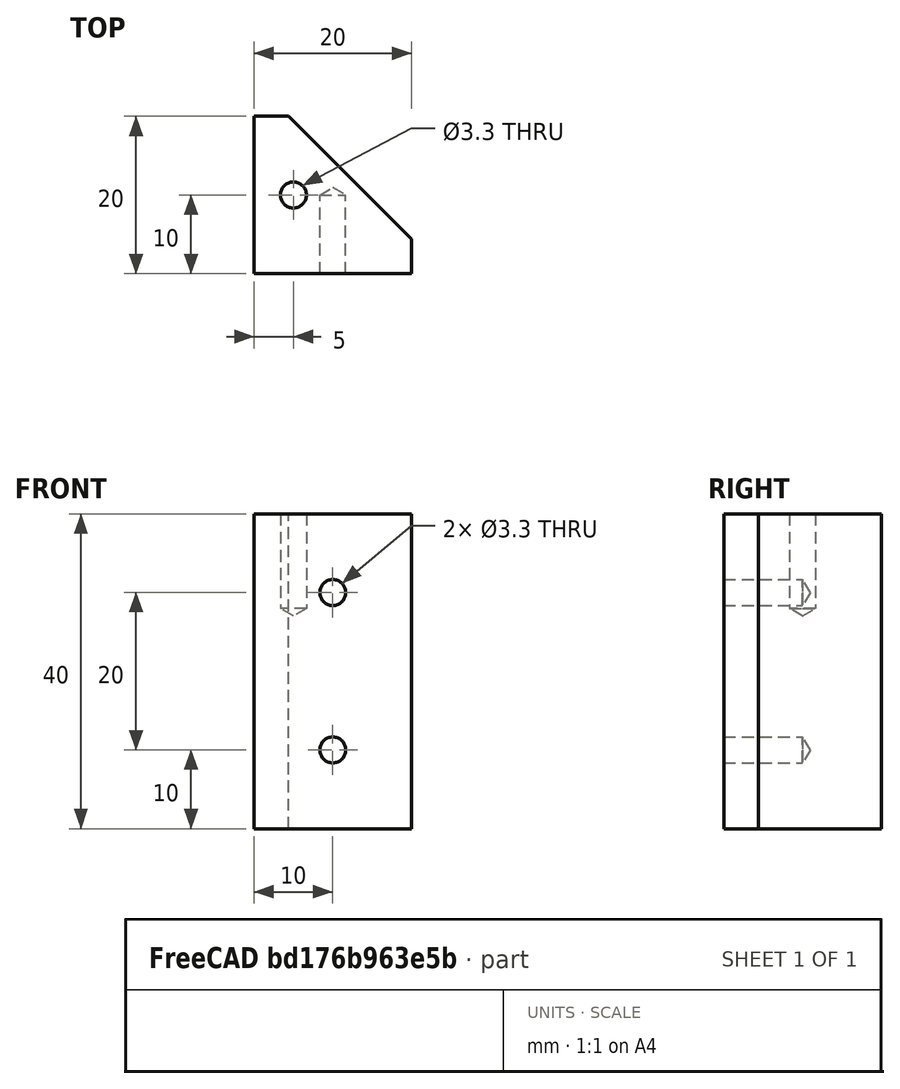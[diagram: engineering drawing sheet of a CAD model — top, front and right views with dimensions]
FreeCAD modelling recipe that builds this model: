
FCSTD DOCUMENT  (FreeCAD 1.0R39319 (Git))
Label: OCT-URBLK-AA
License: Creative Commons Attribution 4.0
LicenseURL: https://creativecommons.org/licenses/by/4.0/
objects: TechDraw::DrawViewDimension×9, Sketcher::SketchObject×3, PartDesign::Hole×2, TechDraw::DrawProjGroupItem×2, PartDesign::Pad×1, PartDesign::Body×1, TechDraw::DrawSVGTemplate×1, TechDraw::DrawProjGroup×1, TechDraw::DrawPage×1
note: 29 computed .brp shape members not serialized (recipe doc carries the construction recipe); baked Part::Feature solids carry a one-line shape summary decoded from their .brp

FEATURE [Sketcher::SketchObject] Sketch
  ArcFitTolerance = 1e-06
  AttachmentSupport = -> [XY_Plane]
  FullyConstrained = true
  MakeInternals = false
  MapMode = 5
  sketch-geometry (5):
    g0: LineSegment StartX=65 StartY=0 StartZ=0 EndX=85 EndY=0 EndZ=0
    g1: LineSegment StartX=85 StartY=0 StartZ=0 EndX=85 EndY=4.4 EndZ=0
    g2: LineSegment StartX=65 StartY=20 StartZ=0 EndX=65 EndY=0 EndZ=0
    g3: LineSegment StartX=65 StartY=20 StartZ=0 EndX=69.4 EndY=20 EndZ=0
    g4: LineSegment StartX=69.4 StartY=20 StartZ=0 EndX=85 EndY=4.4 EndZ=0
  constraints (15):
    c: PointOnObject(g0,g-1)
    c: PointOnObject(g0,g-1)
    c: Coincident(g0,g1)
    c: Vertical(g1)
    c: Vertical(g2)
    c: DistanceX(g0,g0) = 20
    c: DistanceX(g-1,g0) = 85
    c: Coincident(g2,g0)
    c: DistanceY(g2,g2) = 20
    c: Coincident(g2,g3)
    c: Horizontal(g3)
    c: Coincident(g3,g4)
    c: Coincident(g4,g1)
    c: Angle(g4,g0) = 0.785398
    c: DistanceY(g1,g1) = 4.4
FEATURE [PartDesign::Pad] Pad
  Direction = (0,0,1)
  Length = 40
  Length2 = 10
  Profile = -> Sketch
  ReferenceAxis = -> Sketch [N_Axis]
  Suppressed = false
  Type = 0
FEATURE [Sketcher::SketchObject] Sketch001
  ArcFitTolerance = 1e-06
  AttachmentSupport = -> [Pad]
  FullyConstrained = true
  MakeInternals = false
  MapMode = 5
  Placement = pos=(0,0,0) rot=(1,0,0;1.5708rad)
  sketch-geometry (3):
    g0: Circle CenterX=75 CenterY=30 CenterZ=0 NormalX=0 NormalY=0 NormalZ=1 AngleXU=0 Radius=2
    g1: Circle CenterX=75 CenterY=10 CenterZ=0 NormalX=0 NormalY=0 NormalZ=1 AngleXU=0 Radius=2
    g2: LineSegment [constr] StartX=75 StartY=30 StartZ=0 EndX=75 EndY=10 EndZ=0
  constraints (8):
    c: Coincident(g2,g0)
    c: Coincident(g2,g1)
    c: Vertical(g2)
    c: Equal(g0,g1)
    c: Diameter(g0) = 4
    c: DistanceX(g-1,g1) = 75
    c: Distance(g1,g-1) = 10
    c: DistanceY(g2,g2) = 20
FEATURE [PartDesign::Hole] Hole
  BaseFeature = -> Pad
  CustomThreadClearance = 0
  Depth = 10
  DepthType = 0
  Diameter = 3.3
  DrillForDepth = false
  DrillPoint = 1
  DrillPointAngle = 118
  HoleCutCountersinkAngle = 90
  HoleCutCustomValues = false
  HoleCutDepth = 0
  HoleCutDiameter = 6.1
  HoleCutType = 0
  ModelThread = false
  Profile = -> Sketch001
  Suppressed = false
  Tapered = false
  TaperedAngle = 90
  ThreadClass = 0
  ThreadDepth = 10
  ThreadDepthType = 0
  ThreadDirection = 0
  ThreadFit = 0
  ThreadSize = 11
  ThreadType = 1
  Threaded = true
  UseCustomThreadClearance = false
FEATURE [Sketcher::SketchObject] Sketch002
  ArcFitTolerance = 1e-06
  AttachmentSupport = -> [Hole]
  FullyConstrained = true
  MakeInternals = false
  MapMode = 5
  Placement = pos=(0,0,40) rot=(0,0,1;0rad)
  sketch-geometry (1):
    g0: Circle CenterX=70 CenterY=10 CenterZ=0 NormalX=0 NormalY=0 NormalZ=1 AngleXU=0 Radius=2
  constraints (3):
    c: Diameter(g0) = 4
    c: Distance(g0,g-2) = 70
    c: Distance(g0,g-1) = 10
FEATURE [PartDesign::Hole] Hole001
  BaseFeature = -> Hole
  CustomThreadClearance = 0
  Depth = 12
  DepthType = 0
  Diameter = 3.3
  DrillForDepth = false
  DrillPoint = 1
  DrillPointAngle = 118
  HoleCutCountersinkAngle = 90
  HoleCutCustomValues = false
  HoleCutDepth = 0
  HoleCutDiameter = 6.1
  HoleCutType = 0
  ModelThread = false
  Profile = -> Sketch002
  Suppressed = false
  Tapered = false
  TaperedAngle = 90
  ThreadClass = 0
  ThreadDepth = 12
  ThreadDepthType = 0
  ThreadDirection = 0
  ThreadFit = 0
  ThreadSize = 11
  ThreadType = 1
  Threaded = true
  UseCustomThreadClearance = false
FEATURE [PartDesign::Body] Body  label="upper right block"
  AllowCompound = false
  Group = -> [Sketch,Pad,Sketch001,Hole,Sketch002,Hole001]
  Origin = -> Origin
  Tip = -> Hole001
FEATURE [TechDraw::DrawSVGTemplate] Template
  EditableTexts = approval_person=S. Aphelion; creator=Michael Stoll; date_of_issue=08/02/2026; document_status=In preparation; document_type=Component Drawing; drawing_number=DN; general_tolerances=ISO 2768-m; language_code=EN; part_material=Aluminium 6082 T6; responsible_department=RD; revision_index=A; scale=2 : 1; sheet_number=1 / 1; supplementary_title_1=Upper Right Panel Block; title=OCT-URBLK-AA
  Height = 297
  Orientation = 1
  Template = C:/Program Files/FreeCAD 1.0/data/Mod/TechDraw/Templates/A3_Landscape_ISO5457_advanced.svg
  Width = 420
FEATURE [TechDraw::DrawProjGroupItem] View  label="Front"
  CoarseView = false
  Direction = (0,-1,0)
  Focus = 100
  HardHidden = false
  IsoCount = 0
  IsoHidden = false
  IsoVisible = false
  LockPosition = true
  Perspective = false
  Rotation = 0
  RotationVector = (1,0,0)
  Scale = 2
  ScaleType = 2
  ScrubCount = 1
  SeamHidden = false
  SeamVisible = false
  SmoothHidden = false
  SmoothVisible = true
  Source = -> [Body]
  Type = 0
  X = 0
  XDirection = (1,0,0)
  Y = 0
FEATURE [TechDraw::DrawProjGroupItem] ProjItem  label="Top"
  CoarseView = false
  Direction = (0,0,1)
  Focus = 100
  HardHidden = false
  IsoCount = 0
  IsoHidden = false
  IsoVisible = false
  LockPosition = false
  Perspective = false
  Rotation = 0
  RotationVector = (1,0,0)
  Scale = 2
  ScaleType = 0
  ScrubCount = 1
  SeamHidden = false
  SeamVisible = false
  SmoothHidden = false
  SmoothVisible = true
  Source = -> [Body]
  Type = 4
  X = 0
  XDirection = (1,0,0)
  Y = 110
FEATURE [TechDraw::DrawProjGroup] ProjGroup
  Anchor = -> View
  AutoDistribute = true
  LockPosition = false
  ProjectionType = 1
  Rotation = 0
  Scale = 2
  ScaleType = 0
  Source = -> [Body]
  Views = -> [View,ProjItem]
  X = 158.246
  Y = 108.433
  spacingX = 15
  spacingY = 50
FEATURE [TechDraw::DrawViewDimension] Dimension
  AngleOverride = false
  Arbitrary = false
  ArbitraryTolerances = false
  BoxCorners = (2) [(-20,-40,0),(20,40,0)]
  EqualTolerance = true
  ExtensionAngle = 0
  FormatSpec = %.1f
  FormatSpecOverTolerance = %+.1f
  FormatSpecUnderTolerance = %+.1f
  Inverted = false
  LineAngle = 0
  LockPosition = false
  MeasureType = 1
  OverTolerance = 0
  References2D = -> [View]
  Rotation = 0
  Scale = 2
  ScaleType = 0
  TheoreticalExact = false
  Type = 2
  UnderTolerance = 0
  X = 32.4665
  Y = 0
FEATURE [TechDraw::DrawViewDimension] Dimension001
  AngleOverride = false
  Arbitrary = false
  ArbitraryTolerances = false
  BoxCorners = (2) [(-20,-40,0),(20,40,0)]
  EqualTolerance = true
  ExtensionAngle = 0
  FormatSpec = %.1f
  FormatSpecOverTolerance = %+.1f
  FormatSpecUnderTolerance = %+.1f
  Inverted = false
  LineAngle = 0
  LockPosition = false
  MeasureType = 1
  OverTolerance = 0
  References2D = -> [View]
  Rotation = 0
  Scale = 2
  ScaleType = 0
  TheoreticalExact = false
  Type = 1
  UnderTolerance = 0
  X = 0
  Y = -61.7063
FEATURE [TechDraw::DrawViewDimension] Dimension002
  AngleOverride = false
  Arbitrary = false
  ArbitraryTolerances = false
  BoxCorners = (2) [(-20,-40,0),(20,40,0)]
  EqualTolerance = true
  ExtensionAngle = 0
  FormatSpec = %.1f
  FormatSpecOverTolerance = %+.1f
  FormatSpecUnderTolerance = %+.1f
  Inverted = false
  LineAngle = 0
  LockPosition = false
  MeasureType = 1
  OverTolerance = 0
  References2D = -> [View]
  Rotation = 0
  Scale = 2
  ScaleType = 0
  TheoreticalExact = false
  Type = 0
  UnderTolerance = 0
  X = -39.5647
  Y = -30
FEATURE [TechDraw::DrawViewDimension] Dimension003
  AngleOverride = false
  Arbitrary = false
  ArbitraryTolerances = false
  BoxCorners = (2) [(-20,-40,0),(20,40,0)]
  EqualTolerance = true
  ExtensionAngle = 0
  FormatSpec = %.1f
  FormatSpecOverTolerance = %+.1f
  FormatSpecUnderTolerance = %+.1f
  Inverted = false
  LineAngle = 0
  LockPosition = false
  MeasureType = 1
  OverTolerance = 0
  References2D = -> [View]
  Rotation = 0
  Scale = 2
  ScaleType = 0
  TheoreticalExact = false
  Type = 2
  UnderTolerance = 0
  X = -39.5647
  Y = 0
FEATURE [TechDraw::DrawViewDimension] Dimension005
  AngleOverride = false
  Arbitrary = false
  ArbitraryTolerances = false
  BoxCorners = (2) [(-20,-20,0),(20,20,0)]
  EqualTolerance = true
  ExtensionAngle = 0
  FormatSpec = %.1f
  FormatSpecOverTolerance = %+.1f
  FormatSpecUnderTolerance = %+.1f
  Inverted = false
  LineAngle = 0
  LockPosition = false
  MeasureType = 1
  OverTolerance = 0
  References2D = -> [ProjItem]
  Rotation = 0
  Scale = 2
  ScaleType = 0
  TheoreticalExact = false
  Type = 2
  UnderTolerance = 0
  X = -60.5712
  Y = 0
FEATURE [TechDraw::DrawViewDimension] Dimension012
  AngleOverride = false
  Arbitrary = false
  ArbitraryTolerances = false
  BoxCorners = (2) [(-20,-40,0),(20,40,0)]
  EqualTolerance = true
  ExtensionAngle = 0
  FormatSpec = ⌀%.1f
  FormatSpecOverTolerance = %+.1f
  FormatSpecUnderTolerance = %+.1f
  Inverted = false
  LineAngle = 0
  LockPosition = false
  MeasureType = 1
  OverTolerance = 0
  References2D = -> [View]
  Rotation = 0
  Scale = 2
  ScaleType = 0
  TheoreticalExact = false
  Type = 5
  UnderTolerance = 0
  X = -39.8537
  Y = 56.1716
FEATURE [TechDraw::DrawViewDimension] Dimension013
  AngleOverride = false
  Arbitrary = false
  ArbitraryTolerances = false
  BoxCorners = (2) [(-20,-20,0),(20,20,0)]
  EqualTolerance = true
  ExtensionAngle = 0
  FormatSpec = %.1f
  FormatSpecOverTolerance = %+.1f
  FormatSpecUnderTolerance = %+.1f
  Inverted = false
  LineAngle = 0
  LockPosition = false
  MeasureType = 1
  OverTolerance = 0
  References2D = -> [ProjItem]
  Rotation = 0
  Scale = 2
  ScaleType = 0
  TheoreticalExact = false
  Type = 0
  UnderTolerance = 0
  X = 46.6104
  Y = 10
FEATURE [TechDraw::DrawViewDimension] Dimension014
  AngleOverride = false
  Arbitrary = false
  ArbitraryTolerances = false
  BoxCorners = (2) [(-20,-20,0),(20,20,0)]
  EqualTolerance = true
  ExtensionAngle = 0
  FormatSpec = %.1f
  FormatSpecOverTolerance = %+.1f
  FormatSpecUnderTolerance = %+.1f
  Inverted = false
  LineAngle = 0
  LockPosition = false
  MeasureType = 1
  OverTolerance = 0
  References2D = -> [ProjItem]
  Rotation = 0
  Scale = 2
  ScaleType = 0
  TheoreticalExact = false
  Type = 0
  UnderTolerance = 0
  X = -15
  Y = 43.1973
FEATURE [TechDraw::DrawViewDimension] Dimension015
  AngleOverride = false
  Arbitrary = false
  ArbitraryTolerances = false
  BoxCorners = (2) [(-20,-20,0),(20,20,0)]
  EqualTolerance = true
  ExtensionAngle = 0
  FormatSpec = ⌀%.1f
  FormatSpecOverTolerance = %+.1f
  FormatSpecUnderTolerance = %+.1f
  Inverted = false
  LineAngle = 0
  LockPosition = false
  MeasureType = 1
  OverTolerance = 0
  References2D = -> [ProjItem]
  Rotation = 0
  Scale = 2
  ScaleType = 0
  TheoreticalExact = false
  Type = 5
  UnderTolerance = 0
  X = 24.0174
  Y = 49.4019
FEATURE [TechDraw::DrawPage] Page
  KeepUpdated = true
  NextBalloonIndex = 1
  ProjectionType = 1
  Scale = 2
  Template = -> Template
  Views = -> [ProjGroup,Dimension,Dimension001,Dimension002,Dimension003,Dimension005,Dimension012,Dimension013,Dimension014,Dimension015]
